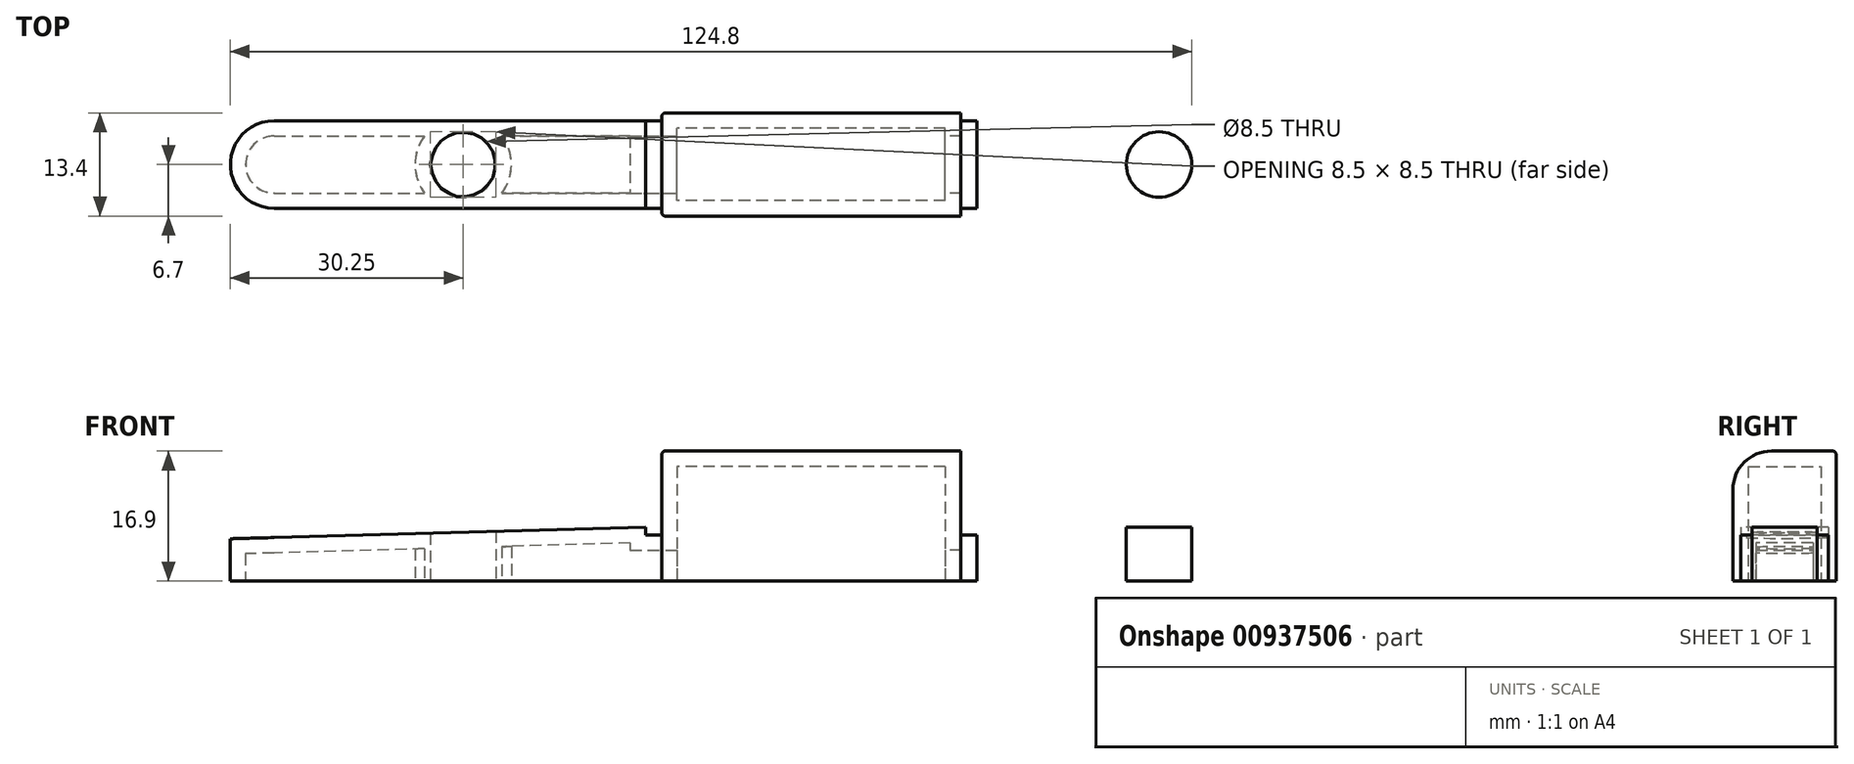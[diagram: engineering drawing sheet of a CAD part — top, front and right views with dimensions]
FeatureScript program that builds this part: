
annotation { "Feature Type Name" : "Feature", "Feature Type Description" : "" }
export const myFeature = defineFeature(function(context is Context, id is Id, definition is map)
    precondition{}
    {
        {
            var Q0;
            Q0=qCreatedBy(makeId("Top.planeOp"),FACE);
            var sketch = newSketch(context, id + "F0", { "sketchPlane" : qUnion([Q0])});
            skLineSegment(sketch, "E0", {"start": v(0, -6.7) * mm, "end": v(-19.4, -6.7) * mm});
            skLineSegment(sketch, "E1", {"start": v(-19.4, -6.7) * mm, "end": v(-19.4, 6.7) * mm});
            skLineSegment(sketch, "E2", {"start": v(-19.4, 6.7) * mm, "end": v(0, 6.7) * mm});
            skLineSegment(sketch, "E3", {"start": v(-19.4, 0) * mm, "end": v(0, 0) * mm, "construction": true});
            skLineSegment(sketch, "E4", {"start": v(-69.7, 5.7) * mm, "end": v(-19.4, 5.7) * mm});
            skLineSegment(sketch, "E5", {"start": v(-69.7, -5.7) * mm, "end": v(-19.4, -5.7) * mm});
            skArc(sketch, "E6", {"start": v(-69.7, 5.7) * mm, "mid": v(-75.4, 0) * mm, "end": v(-69.7, -5.7) * mm});
            skLineSegment(sketch, "E7", {"start": v(-21.5, 5.7) * mm, "end": v(-21.5, -5.7) * mm});
            skLineSegment(sketch, "E8", {"start": v(-21.5, 0) * mm, "end": v(-19.4, 0) * mm, "construction": true});
            skLineSegment(sketch, "E9", {"start": v(0, 23.84) * mm, "end": v(0, -27.02) * mm, "construction": true});
            skCircle(sketch, "E10", {"center": v(-45.15, 0) * mm, "radius": 4.25 * mm});
            skLineSegment(sketch, "E11.MirrorCS", {"start": v(21.5, 0) * mm, "end": v(19.4, 0) * mm, "construction": true});
            skLineSegment(sketch, "E12.MirrorCS", {"start": v(19.4, 0) * mm, "end": v(0, 0) * mm, "construction": true});
            skCircle(sketch, "E13.MirrorC", {"center": v(45.15, 0) * mm, "radius": 4.25 * mm});
            skLineSegment(sketch, "E14.MirrorCS", {"start": v(19.4, -6.7) * mm, "end": v(19.4, 6.7) * mm});
            skArc(sketch, "E15.MirrorCS", {"start": v(69.7, 5.7) * mm, "mid": v(75.4, 0) * mm, "end": v(69.7, -5.7) * mm});
            skLineSegment(sketch, "E16.MirrorCS", {"start": v(69.7, -5.7) * mm, "end": v(19.4, -5.7) * mm});
            skLineSegment(sketch, "E17.MirrorCS", {"start": v(19.4, 6.7) * mm, "end": v(0, 6.7) * mm});
            skLineSegment(sketch, "E18.MirrorCS", {"start": v(0, -6.7) * mm, "end": v(19.4, -6.7) * mm});
            skLineSegment(sketch, "E19.MirrorCS", {"start": v(69.7, 5.7) * mm, "end": v(19.4, 5.7) * mm});
            skLineSegment(sketch, "E20.MirrorCS", {"start": v(21.5, 5.7) * mm, "end": v(21.5, -5.7) * mm});
            skSolve(sketch);
        }
        {
            var Q0;
            {var subQ4=sQuery(id+"F0.wireOp",EDGE,"E0");Q0=makeQuery(id+"F0.imprint","IMPRINT",FACE,{"disambiguationData":[TD([[makeQuery(id+"F0.imprint","IMPRINT",EDGE,{"derivedFrom":subQ4}),-1.0]])]});}
            extrude(context, id + "F1", {"entities" : qUnion([Q0]), "flatOperationType" : FlatOperationType.REMOVE, "depth" : 16.9 * mm, "offsetDistance" : 25 * mm, "domain" : OperationDomain.MODEL});
        }
        {
            var Q0;
            {var subQ5=sQuery(id+"F0.wireOp",EDGE,"E7");Q0=makeQuery(id+"F0.imprint","IMPRINT",FACE,{"disambiguationData":[TD([[makeQuery(id+"F0.imprint","IMPRINT",EDGE,{"derivedFrom":subQ5}),1.0]])]});}
            var Q1;
            {var subQ5=sQuery(id+"F0.wireOp",EDGE,"E20.MirrorCS");Q1=makeQuery(id+"F0.imprint","IMPRINT",FACE,{"disambiguationData":[TD([[makeQuery(id+"F0.imprint","IMPRINT",EDGE,{"derivedFrom":subQ5}),-1.0]])]});}
            extrude(context, id + "F2", {"entities" : qUnion([Q0, Q1]), "operationType" : NewBodyOperationType.ADD, "flatOperationType" : FlatOperationType.REMOVE, "depth" : 6 * mm, "offsetDistance" : 25 * mm, "domain" : OperationDomain.MODEL});
        }
        {
            var Q0;
            {var subQ0=sQuery(id+"F0.wireOp",EDGE,"E6");Q0=makeQuery(id+"F0.imprint","IMPRINT",FACE,{"disambiguationData":[TD([[makeQuery(id+"F0.imprint","IMPRINT",EDGE,{"derivedFrom":subQ0}),1.0]])]});}
            var Q1;
            Q1=makeQuery(id+"F0.imprint","IMPRINT",FACE,{"disambiguationData":[TD([[makeQuery(id+"F0.imprint","IMPRINT",EDGE,{"derivedFrom":sQuery(id+"F0.wireOp",EDGE,"E13.MirrorC")}),1.0]])]});
            extrude(context, id + "F3", {"entities" : qUnion([Q0, Q1]), "operationType" : NewBodyOperationType.ADD, "flatOperationType" : FlatOperationType.REMOVE, "depth" : 7 * mm, "offsetDistance" : 25 * mm, "domain" : OperationDomain.MODEL});
        }
        {
            var Q0;
            {var subQ0=sQuery(id+"F0.wireOp",EDGE,"E5");Q0=makeQuery(id+"F3.boolean.opBoolean","MERGE",FACE,{"derivedFrom":[makeQuery(id+"F2.opExtrude","SWEPT_FACE",FACE,{"disambiguationData":[OSD([subQ0])]}),makeQuery(id+"F3.opExtrude","SWEPT_FACE",FACE,{"disambiguationData":[OSD([subQ0])]})]});}
            var sketch = newSketch(context, id + "F4", { "sketchPlane" : qUnion([Q0])});
            skLineSegment(sketch, "E21", {"start": v(-75.4, 0) * mm, "end": v(-75.4, 5.5) * mm, "construction": true});
            skLineSegment(sketch, "E22", {"start": v(-21.5, 7) * mm, "end": v(-75.4, 7) * mm});
            skLineSegment(sketch, "E23", {"start": v(-75.4, 7) * mm, "end": v(-75.4, 5.5) * mm});
            skLineSegment(sketch, "E24", {"start": v(-21.5, 7) * mm, "end": v(-75.4, 5.5) * mm});
            skSolve(sketch);
        }
        {
            var Q0;
            {var subQ0=sQuery(id+"F4.wireOp",EDGE,"E22");var subQ1=sQuery(id+"F0.wireOp",EDGE,"E5");var subQ4=sQuery(id+"F4.wireOp",EDGE,"E24");var subQ5=makeQuery(id+"F4.imprint","INTERSECT",VERTEX,{"derivedFrom":[makeQuery(id+"F3.opExtrude","SWEPT_EDGE",EDGE,{"disambiguationData":[OSD([subQ1,sQuery(id+"F0.wireOp",EDGE,"E7")])]}),subQ0,subQ4]});Q0=makeQuery(id+"F4.imprint","IMPRINT",FACE,{"disambiguationData":[TD([[makeQuery(id+"F4.imprint","IMPRINT",EDGE,{"disambiguationData":[TD([[subQ5,1.0]])],"derivedFrom":subQ0}),-1.0]])]});}
            var Q1;
            {var subQ3=sQuery(id+"F4.wireOp",EDGE,"E23");Q1=makeQuery(id+"F4.imprint","IMPRINT",FACE,{"disambiguationData":[TD([[makeQuery(id+"F4.imprint","IMPRINT",EDGE,{"derivedFrom":subQ3}),1.0]])]});}
            var Q2;
            {var subQ0=sQuery(id+"F0.wireOp",EDGE,"E4");Q2=makeQuery(id+"F3.boolean.opBoolean","MERGE",FACE,{"derivedFrom":[makeQuery(id+"F2.opExtrude","SWEPT_FACE",FACE,{"disambiguationData":[OSD([subQ0])]}),makeQuery(id+"F3.opExtrude","SWEPT_FACE",FACE,{"disambiguationData":[OSD([subQ0])]})]});}
            extrude(context, id + "F5", {"entities" : qUnion([Q0, Q1]), "operationType" : NewBodyOperationType.REMOVE, "endBound" : BoundingType.UP_TO_SURFACE, "oppositeDirection" : true, "depth" : 25 * mm, "endBoundEntityFace" : qUnion([Q2]), "offsetDistance" : 25 * mm});
        }
        {
            var Q0;
            {var subQ0=sQuery(id+"F0.wireOp",EDGE,"1f06ee96-7bfd-495a-a702-5e96e6a737e410.MirrorCS");var subQ1=sQuery(id+"F0.wireOp",EDGE,"1f06ee96-7bfd-495a-a702-5e96e6a737e42.MirrorCS");var subQ2=sQuery(id+"F0.wireOp",EDGE,"1f06ee96-7bfd-495a-a702-5e96e6a737e41.MirrorCS");var subQ3=sQuery(id+"F0.wireOp",EDGE,"E7");var subQ4=sQuery(id+"F0.wireOp",EDGE,"E5");var subQ5=sQuery(id+"F0.wireOp",EDGE,"E4");var subQ6=sQuery(id+"F0.wireOp",EDGE,"ceafb676-a6cf-4187-bdd4-0307e78c99340.MirrorCS");var subQ7=sQuery(id+"F0.wireOp",EDGE,"E1");Q0=makeQuery(id+"FK2SPu7BtQZRUrj_0.boolean.opBoolean","MERGE",FACE,{"derivedFrom":[makeQuery(id+"FKIXRtlMRZzBrNx_0.boolean.opBoolean","MERGE",FACE,{"derivedFrom":[makeQuery(id+"F1.opExtrude","CAP_FACE",FACE,{"disambiguationData":[OSD([sQuery(id+"F0.wireOp",EDGE,"E0"),subQ7,sQuery(id+"F0.wireOp",EDGE,"E2"),sQuery(id+"F0.wireOp",EDGE,"1f06ee96-7bfd-495a-a702-5e96e6a737e49.MirrorCS"),sQuery(id+"F0.wireOp",EDGE,"1f06ee96-7bfd-495a-a702-5e96e6a737e411.MirrorCS"),subQ6])],"isStart":true}),makeQuery(id+"FKIXRtlMRZzBrNx_0.opExtrude","CAP_FACE",FACE,{"disambiguationData":[OSD([subQ7,subQ5,subQ4,subQ3])],"isStart":true}),makeQuery(id+"FKIXRtlMRZzBrNx_0.opExtrude","CAP_FACE",FACE,{"disambiguationData":[OSD([subQ2,subQ1,subQ0,subQ6])],"isStart":true})]}),makeQuery(id+"FK2SPu7BtQZRUrj_0.opExtrude","CAP_FACE",FACE,{"disambiguationData":[OSD([subQ5,subQ4,sQuery(id+"F0.wireOp",EDGE,"djeqks3d-ucOt-0V9V-x2zC-lVN3i5GyaOPg"),sQuery(id+"F0.wireOp",EDGE,"E6"),subQ3])],"isStart":true}),makeQuery(id+"FK2SPu7BtQZRUrj_0.opExtrude","CAP_FACE",FACE,{"disambiguationData":[OSD([subQ2,subQ1,sQuery(id+"F0.wireOp",EDGE,"1f06ee96-7bfd-495a-a702-5e96e6a737e45.MirrorC"),sQuery(id+"F0.wireOp",EDGE,"1f06ee96-7bfd-495a-a702-5e96e6a737e47.MirrorCS"),subQ0])],"isStart":true})]});}
            shell(context, id + "F6", {"entities" : qUnion([Q0]), "thickness" : 2 * mm});
        }
        {
            var Q0;
            Q0=makeQuery(id+"F1.opExtrude","CAP_EDGE",EDGE,{"disambiguationData":[OSD([sQuery(id+"F0.wireOp",EDGE,"E0"),sQuery(id+"F0.wireOp",EDGE,"1f06ee96-7bfd-495a-a702-5e96e6a737e49.MirrorCS")])],"isStart":false});
            var Q1;
            Q1=makeQuery(id+"FXeT8B0WGAwKg6D_1.opFillet","BLEND_EDGE",EDGE,{"blendedFrom":[makeQuery(id+"F1.opExtrude","CAP_EDGE",EDGE,{"disambiguationData":[OSD([sQuery(id+"F0.wireOp",EDGE,"ceafb676-a6cf-4187-bdd4-0307e78c99340.MirrorCS")])],"isStart":false}),makeQuery(id+"F1.opExtrude","SWEPT_FACE",FACE,{"disambiguationData":[OSD([sQuery(id+"F0.wireOp",EDGE,"E0"),sQuery(id+"F0.wireOp",EDGE,"1f06ee96-7bfd-495a-a702-5e96e6a737e49.MirrorCS")])]})],"blendedInto":[makeQuery(id+"F1.opExtrude","SWEPT_FACE",FACE,{"disambiguationData":[OSD([sQuery(id+"F0.wireOp",EDGE,"E0"),sQuery(id+"F0.wireOp",EDGE,"1f06ee96-7bfd-495a-a702-5e96e6a737e49.MirrorCS")])]})]});
            var Q2;
            Q2=makeQuery(id+"FXeT8B0WGAwKg6D_1.opFillet","BLEND_EDGE",EDGE,{"blendedFrom":[makeQuery(id+"F1.opExtrude","CAP_EDGE",EDGE,{"disambiguationData":[OSD([sQuery(id+"F0.wireOp",EDGE,"E1")])],"isStart":false}),makeQuery(id+"F1.opExtrude","SWEPT_FACE",FACE,{"disambiguationData":[OSD([sQuery(id+"F0.wireOp",EDGE,"E0"),sQuery(id+"F0.wireOp",EDGE,"1f06ee96-7bfd-495a-a702-5e96e6a737e49.MirrorCS")])]})],"blendedInto":[makeQuery(id+"F1.opExtrude","SWEPT_FACE",FACE,{"disambiguationData":[OSD([sQuery(id+"F0.wireOp",EDGE,"E0"),sQuery(id+"F0.wireOp",EDGE,"1f06ee96-7bfd-495a-a702-5e96e6a737e49.MirrorCS")])]})]});
            fillet(context, id + "F7", {"entities" : qUnion([Q0, Q1, Q2]), "radius" : 5 * mm, "tangentPropagation" : true, "allowEdgeOverflow" : false});
        }
        {
            var Q0;
            Q0=makeQuery(id+"F1.opExtrude","CAP_EDGE",EDGE,{"disambiguationData":[OSD([sQuery(id+"F0.wireOp",EDGE,"E1")])],"isStart":false});
            var Q1;
            Q1=makeQuery(id+"F1.opExtrude","CAP_EDGE",EDGE,{"disambiguationData":[OSD([sQuery(id+"F0.wireOp",EDGE,"E2"),sQuery(id+"F0.wireOp",EDGE,"1f06ee96-7bfd-495a-a702-5e96e6a737e411.MirrorCS")])],"isStart":false});
            var Q2;
            Q2=makeQuery(id+"F1.opExtrude","CAP_EDGE",EDGE,{"disambiguationData":[OSD([sQuery(id+"F0.wireOp",EDGE,"ceafb676-a6cf-4187-bdd4-0307e78c99340.MirrorCS")])],"isStart":false});
            var Q3;
            Q3=makeQuery(id+"F7.opFillet","BLEND_EDGE",EDGE,{"blendedFrom":[makeQuery(id+"F1.opExtrude","CAP_EDGE",EDGE,{"disambiguationData":[OSD([sQuery(id+"F0.wireOp",EDGE,"E0"),sQuery(id+"F0.wireOp",EDGE,"1f06ee96-7bfd-495a-a702-5e96e6a737e49.MirrorCS")])],"isStart":false}),makeQuery(id+"F1.opExtrude","SWEPT_FACE",FACE,{"disambiguationData":[OSD([sQuery(id+"F0.wireOp",EDGE,"E1")])]})],"blendedInto":[makeQuery(id+"F1.opExtrude","SWEPT_FACE",FACE,{"disambiguationData":[OSD([sQuery(id+"F0.wireOp",EDGE,"E1")])]})]});
            var Q4;
            Q4=makeQuery(id+"F7.opFillet","BLEND_EDGE",EDGE,{"blendedFrom":[makeQuery(id+"F1.opExtrude","CAP_EDGE",EDGE,{"disambiguationData":[OSD([sQuery(id+"F0.wireOp",EDGE,"E0"),sQuery(id+"F0.wireOp",EDGE,"1f06ee96-7bfd-495a-a702-5e96e6a737e49.MirrorCS")])],"isStart":false}),makeQuery(id+"F1.opExtrude","SWEPT_FACE",FACE,{"disambiguationData":[OSD([sQuery(id+"F0.wireOp",EDGE,"ceafb676-a6cf-4187-bdd4-0307e78c99340.MirrorCS")])]})],"blendedInto":[makeQuery(id+"F1.opExtrude","SWEPT_FACE",FACE,{"disambiguationData":[OSD([sQuery(id+"F0.wireOp",EDGE,"ceafb676-a6cf-4187-bdd4-0307e78c99340.MirrorCS")])]})]});
            var Q5;
            Q5=makeQuery(id+"F1.opExtrude","SWEPT_EDGE",EDGE,{"disambiguationData":[OSD([sQuery(id+"F0.wireOp",EDGE,"E0"),sQuery(id+"F0.wireOp",EDGE,"E1")])]});
            var Q6;
            Q6=makeQuery(id+"F1.opExtrude","SWEPT_EDGE",EDGE,{"disambiguationData":[OSD([sQuery(id+"F0.wireOp",EDGE,"1f06ee96-7bfd-495a-a702-5e96e6a737e49.MirrorCS"),sQuery(id+"F0.wireOp",EDGE,"ceafb676-a6cf-4187-bdd4-0307e78c99340.MirrorCS")])]});
            var Q7;
            Q7=makeQuery(id+"FzKwIEV41N3puCh_1.boolean.opBoolean","COPY",EDGE,{"derivedFrom":makeQuery(id+"FzKwIEV41N3puCh_1.opExtrude","CAP_EDGE",EDGE,{"disambiguationData":[OSD([sQuery(id+"FuPS0Dc4K56yM07_1.wireOp",EDGE,"KalmSChX-J7J4-kyIO-l68x-muKg0xG4JHzr")])],"isStart":true})});
            var Q8;
            {var subQ0=sQuery(id+"F0.wireOp",EDGE,"E7");Q8=makeQuery(id+"FzKwIEV41N3puCh_1.boolean.opBoolean","MERGE",EDGE,{"derivedFrom":[makeQuery(id+"FK2SPu7BtQZRUrj_0.opExtrude","CAP_EDGE",EDGE,{"disambiguationData":[OSD([subQ0])],"isStart":false})],"fromTools":[makeQuery(id+"FzKwIEV41N3puCh_1.opExtrude","SWEPT_EDGE",EDGE,{"disambiguationData":[OSD([sQuery(id+"F0.wireOp",EDGE,"E5"),subQ0,sQuery(id+"FuPS0Dc4K56yM07_1.wireOp",EDGE,"PpaWvTEU-qsYT-PJ9n-Q8D4-rOtRaajH0fIj"),sQuery(id+"FuPS0Dc4K56yM07_1.wireOp",EDGE,"KalmSChX-J7J4-kyIO-l68x-muKg0xG4JHzr")])]})]});}
            var Q9;
            Q9=makeQuery(id+"FzKwIEV41N3puCh_1.boolean.opBoolean","COPY",EDGE,{"derivedFrom":makeQuery(id+"FzKwIEV41N3puCh_1.opExtrude","CAP_EDGE",EDGE,{"disambiguationData":[OSD([sQuery(id+"FuPS0Dc4K56yM07_1.wireOp",EDGE,"KalmSChX-J7J4-kyIO-l68x-muKg0xG4JHzr")])],"isStart":false})});
            var Q10;
            Q10=makeQuery(id+"FzKwIEV41N3puCh_1.boolean.opBoolean","INTERSECT",EDGE,{"derivedFrom":[makeQuery(id+"FK2SPu7BtQZRUrj_0.opExtrude","SWEPT_FACE",FACE,{"disambiguationData":[OSD([sQuery(id+"F0.wireOp",EDGE,"E6")])]}),makeQuery(id+"FzKwIEV41N3puCh_1.opExtrude","SWEPT_FACE",FACE,{"disambiguationData":[OSD([sQuery(id+"FuPS0Dc4K56yM07_1.wireOp",EDGE,"KalmSChX-J7J4-kyIO-l68x-muKg0xG4JHzr")])]})]});
            var Q11;
            Q11=makeQuery(id+"FUvFt8S9zfStnt9_1.1.FzKwIEV41N3puCh_1.boolean.opBoolean","COPY",EDGE,{"derivedFrom":makeQuery(id+"FUvFt8S9zfStnt9_1.1.FzKwIEV41N3puCh_1.opExtrude","CAP_EDGE",EDGE,{"disambiguationData":[OSD([sQuery(id+"FuPS0Dc4K56yM07_1.wireOp",EDGE,"KalmSChX-J7J4-kyIO-l68x-muKg0xG4JHzr")])],"isStart":true})});
            var Q12;
            Q12=makeQuery(id+"FUvFt8S9zfStnt9_1.1.FzKwIEV41N3puCh_1.boolean.opBoolean","INTERSECT",EDGE,{"derivedFrom":[makeQuery(id+"FK2SPu7BtQZRUrj_0.opExtrude","SWEPT_FACE",FACE,{"disambiguationData":[OSD([sQuery(id+"F0.wireOp",EDGE,"1f06ee96-7bfd-495a-a702-5e96e6a737e47.MirrorCS")])]}),makeQuery(id+"FUvFt8S9zfStnt9_1.1.FzKwIEV41N3puCh_1.opExtrude","SWEPT_FACE",FACE,{"disambiguationData":[OSD([sQuery(id+"FuPS0Dc4K56yM07_1.wireOp",EDGE,"KalmSChX-J7J4-kyIO-l68x-muKg0xG4JHzr")])]})]});
            var Q13;
            Q13=makeQuery(id+"FUvFt8S9zfStnt9_1.1.FzKwIEV41N3puCh_1.boolean.opBoolean","COPY",EDGE,{"derivedFrom":makeQuery(id+"FUvFt8S9zfStnt9_1.1.FzKwIEV41N3puCh_1.opExtrude","CAP_EDGE",EDGE,{"disambiguationData":[OSD([sQuery(id+"FuPS0Dc4K56yM07_1.wireOp",EDGE,"KalmSChX-J7J4-kyIO-l68x-muKg0xG4JHzr")])],"isStart":false})});
            var Q14;
            Q14=makeQuery(id+"FK2SPu7BtQZRUrj_0.opExtrude","SWEPT_EDGE",EDGE,{"disambiguationData":[OSD([sQuery(id+"F0.wireOp",EDGE,"1f06ee96-7bfd-495a-a702-5e96e6a737e41.MirrorCS"),sQuery(id+"F0.wireOp",EDGE,"1f06ee96-7bfd-495a-a702-5e96e6a737e42.MirrorCS")])]});
            var Q15;
            Q15=makeQuery(id+"FK2SPu7BtQZRUrj_0.opExtrude","SWEPT_EDGE",EDGE,{"disambiguationData":[OSD([sQuery(id+"F0.wireOp",EDGE,"E4"),sQuery(id+"F0.wireOp",EDGE,"E7")])]});
            var Q16;
            Q16=makeQuery(id+"FK2SPu7BtQZRUrj_0.opExtrude","SWEPT_EDGE",EDGE,{"disambiguationData":[OSD([sQuery(id+"F0.wireOp",EDGE,"1f06ee96-7bfd-495a-a702-5e96e6a737e42.MirrorCS"),sQuery(id+"F0.wireOp",EDGE,"1f06ee96-7bfd-495a-a702-5e96e6a737e410.MirrorCS")])]});
            var Q17;
            Q17=makeQuery(id+"FK2SPu7BtQZRUrj_0.opExtrude","SWEPT_EDGE",EDGE,{"disambiguationData":[OSD([sQuery(id+"F0.wireOp",EDGE,"E5"),sQuery(id+"F0.wireOp",EDGE,"E7")])]});
            var Q18;
            Q18=makeQuery(id+"F1.opExtrude","SWEPT_EDGE",EDGE,{"disambiguationData":[OSD([sQuery(id+"F0.wireOp",EDGE,"E1"),sQuery(id+"F0.wireOp",EDGE,"E2")])]});
            var Q19;
            Q19=makeQuery(id+"F1.opExtrude","SWEPT_EDGE",EDGE,{"disambiguationData":[OSD([sQuery(id+"F0.wireOp",EDGE,"1f06ee96-7bfd-495a-a702-5e96e6a737e411.MirrorCS"),sQuery(id+"F0.wireOp",EDGE,"ceafb676-a6cf-4187-bdd4-0307e78c99340.MirrorCS")])]});
            var Q20;
            Q20=makeQuery(id+"FUvFt8S9zfStnt9_1.1.FzKwIEV41N3puCh_1.boolean.opBoolean","MERGE",EDGE,{"derivedFrom":[makeQuery(id+"FK2SPu7BtQZRUrj_0.opExtrude","CAP_EDGE",EDGE,{"disambiguationData":[OSD([sQuery(id+"F0.wireOp",EDGE,"1f06ee96-7bfd-495a-a702-5e96e6a737e42.MirrorCS")])],"isStart":false})],"fromTools":[makeQuery(id+"FUvFt8S9zfStnt9_1.1.FzKwIEV41N3puCh_1.opExtrude","SWEPT_EDGE",EDGE,{"disambiguationData":[OSD([sQuery(id+"F0.wireOp",EDGE,"E5"),sQuery(id+"F0.wireOp",EDGE,"E7"),sQuery(id+"FuPS0Dc4K56yM07_1.wireOp",EDGE,"PpaWvTEU-qsYT-PJ9n-Q8D4-rOtRaajH0fIj"),sQuery(id+"FuPS0Dc4K56yM07_1.wireOp",EDGE,"KalmSChX-J7J4-kyIO-l68x-muKg0xG4JHzr")])]})]});
            fillet(context, id + "F8", {"entities" : qUnion([Q0, Q1, Q2, Q3, Q4, Q5, Q6, Q7, Q8, Q9, Q10, Q11, Q12, Q13, Q14, Q15, Q16, Q17, Q18, Q19, Q20]), "radius" : 0.5 * mm, "allowEdgeOverflow" : false});
        }
    });
